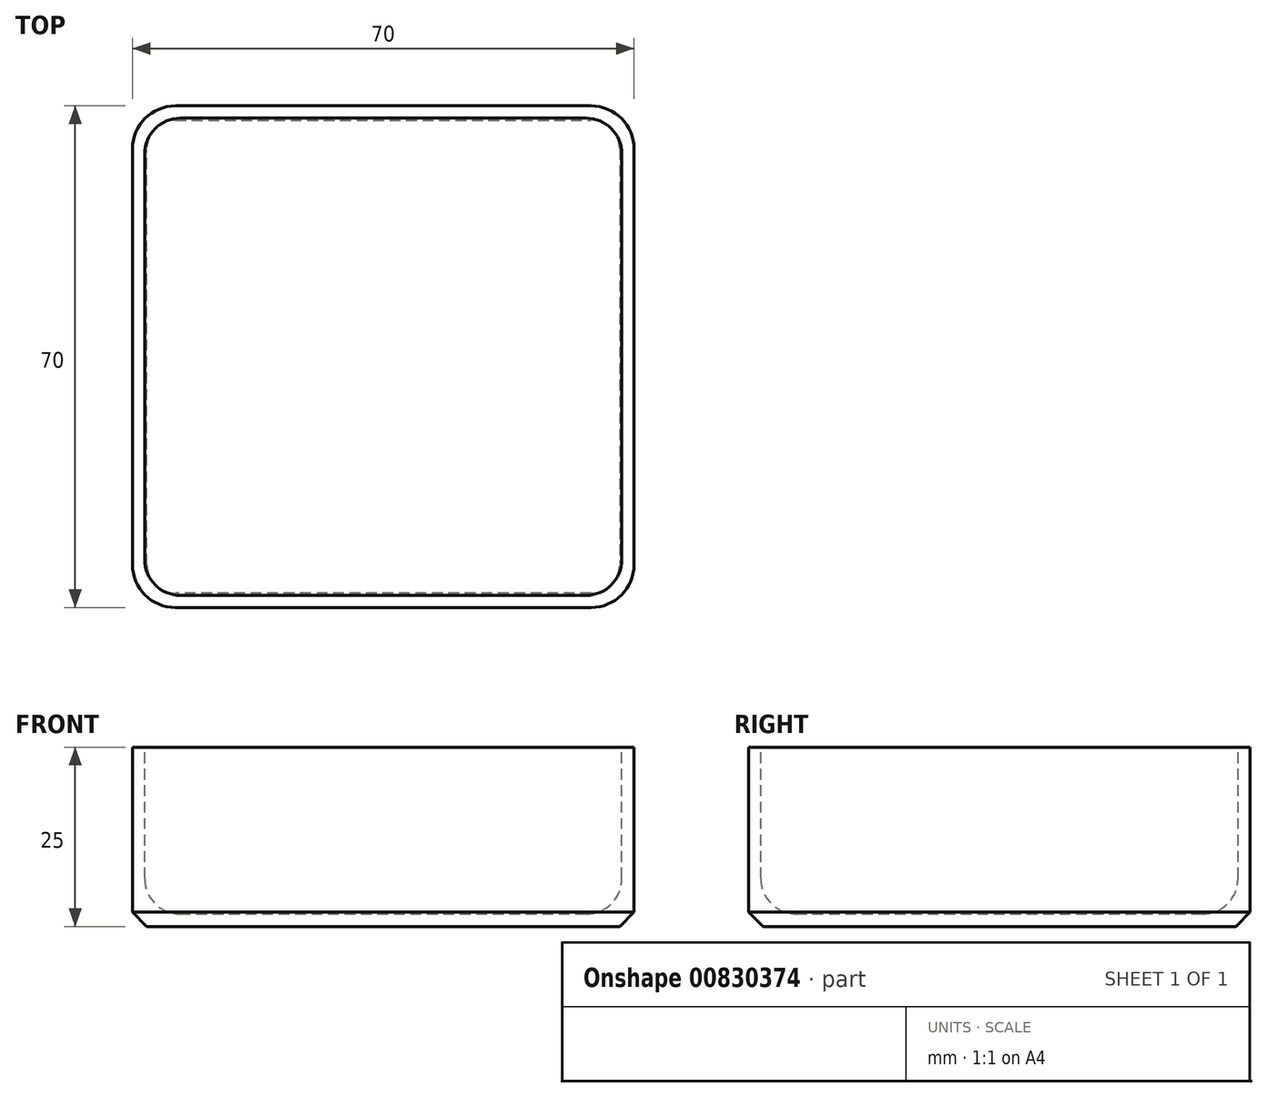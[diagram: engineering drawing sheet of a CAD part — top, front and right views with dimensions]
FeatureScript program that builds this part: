
annotation { "Feature Type Name" : "Feature", "Feature Type Description" : "" }
export const myFeature = defineFeature(function(context is Context, id is Id, definition is map)
    precondition{}
    {
        {
            var Q0;
            Q0=qCreatedBy(makeId("Top.planeOp"),FACE);
            var sketch = newSketch(context, id + "F0", { "sketchPlane" : qUnion([Q0])});
            skLineSegment(sketch, "E0.bottom", {"start": v(35, 35) * mm, "end": v(-35, 35) * mm});
            skLineSegment(sketch, "E0.top", {"start": v(35, -35) * mm, "end": v(-35, -35) * mm});
            skLineSegment(sketch, "E0.left", {"start": v(35, 35) * mm, "end": v(35, -35) * mm});
            skLineSegment(sketch, "E0.right", {"start": v(-35, 35) * mm, "end": v(-35, -35) * mm});
            skPoint(sketch, "E0.middle", {"position": v(0, 0) * mm});
            skLineSegment(sketch, "E1.bottom", {"start": v(33.3, 33.3) * mm, "end": v(-33.3, 33.3) * mm});
            skLineSegment(sketch, "E1.top", {"start": v(33.3, -33.3) * mm, "end": v(-33.3, -33.3) * mm});
            skLineSegment(sketch, "E1.left", {"start": v(33.3, 33.3) * mm, "end": v(33.3, -33.3) * mm});
            skLineSegment(sketch, "E1.right", {"start": v(-33.3, 33.3) * mm, "end": v(-33.3, -33.3) * mm});
            skSolve(sketch);
        }
        {
            var Q0;
            Q0=makeQuery(id+"F0.imprint","IMPRINT",FACE,{"disambiguationData":[TD([[makeQuery(id+"F0.imprint","IMPRINT",EDGE,{"derivedFrom":sQuery(id+"F0.wireOp",EDGE,"E1.bottom")}),1.0]])]});
            var Q1;
            Q1 = qSketchRegion(id + "F0", true);
            var Q2;
            Q2=makeQuery(id+"F0.imprint","IMPRINT",FACE,{"disambiguationData":[TD([[makeQuery(id+"F0.imprint","IMPRINT",EDGE,{"derivedFrom":sQuery(id+"F0.wireOp",EDGE,"E0.bottom")}),1.0]])]});
            extrude(context, id + "F1", {"entities" : qUnion([Q0, Q1, Q2]), "depth" : 25 * mm, "offsetDistance" : 25 * mm});
        }
        {
            var Q0;
            Q0=makeQuery(id+"F1.opExtrude","CAP_FACE",FACE,{"disambiguationData":[OSD([sQuery(id+"F0.wireOp",EDGE,"E0.bottom"),sQuery(id+"F0.wireOp",EDGE,"E0.top"),sQuery(id+"F0.wireOp",EDGE,"E0.left"),sQuery(id+"F0.wireOp",EDGE,"E0.right")])],"isStart":false});
            var sketch = newSketch(context, id + "F2", { "sketchPlane" : qUnion([Q0])});
            skLineSegment(sketch, "E2.bottom", {"start": v(33.3, 33.3) * mm, "end": v(-33.3, 33.3) * mm});
            skLineSegment(sketch, "E2.top", {"start": v(33.3, -33.3) * mm, "end": v(-33.3, -33.3) * mm});
            skLineSegment(sketch, "E2.left", {"start": v(33.3, 33.3) * mm, "end": v(33.3, -33.3) * mm});
            skLineSegment(sketch, "E2.right", {"start": v(-33.3, 33.3) * mm, "end": v(-33.3, -33.3) * mm});
            skPoint(sketch, "E2.middle", {"position": v(0, 0) * mm});
            skSolve(sketch);
        }
        {
            var Q0;
            Q0=makeQuery(id+"F2.imprint","IMPRINT",FACE,{"disambiguationData":[TD([[makeQuery(id+"F2.imprint","IMPRINT",EDGE,{"derivedFrom":sQuery(id+"F2.wireOp",EDGE,"E2.bottom")}),1.0]])]});
            extrude(context, id + "F3", {"entities" : qUnion([Q0]), "operationType" : NewBodyOperationType.REMOVE, "oppositeDirection" : true, "depth" : 23.3 * mm, "offsetDistance" : 25 * mm});
        }
        {
            var Q0;
            Q0=makeQuery(id+"F3.boolean.opBoolean","COPY",EDGE,{"derivedFrom":makeQuery(id+"F3.opExtrude","CAP_EDGE",EDGE,{"disambiguationData":[OSD([sQuery(id+"F2.wireOp",EDGE,"E2.right")])],"isStart":false})});
            var Q1;
            Q1=makeQuery(id+"F3.boolean.opBoolean","COPY",EDGE,{"derivedFrom":makeQuery(id+"F3.opExtrude","CAP_EDGE",EDGE,{"disambiguationData":[OSD([sQuery(id+"F2.wireOp",EDGE,"E2.left")])],"isStart":false})});
            var Q2;
            Q2=makeQuery(id+"F3.boolean.opBoolean","COPY",EDGE,{"derivedFrom":makeQuery(id+"F3.opExtrude","SWEPT_EDGE",EDGE,{"disambiguationData":[OSD([sQuery(id+"F2.wireOp",EDGE,"E2.bottom"),sQuery(id+"F2.wireOp",EDGE,"E2.right")])]})});
            var Q3;
            Q3=makeQuery(id+"F3.boolean.opBoolean","COPY",EDGE,{"derivedFrom":makeQuery(id+"F3.opExtrude","CAP_EDGE",EDGE,{"disambiguationData":[OSD([sQuery(id+"F2.wireOp",EDGE,"E2.bottom")])],"isStart":false})});
            var Q4;
            Q4=makeQuery(id+"F3.boolean.opBoolean","COPY",EDGE,{"derivedFrom":makeQuery(id+"F3.opExtrude","SWEPT_EDGE",EDGE,{"disambiguationData":[OSD([sQuery(id+"F2.wireOp",EDGE,"E2.top"),sQuery(id+"F2.wireOp",EDGE,"E2.right")])]})});
            var Q5;
            Q5=makeQuery(id+"F3.boolean.opBoolean","COPY",EDGE,{"derivedFrom":makeQuery(id+"F3.opExtrude","CAP_EDGE",EDGE,{"disambiguationData":[OSD([sQuery(id+"F2.wireOp",EDGE,"E2.top")])],"isStart":false})});
            var Q6;
            Q6=makeQuery(id+"F3.boolean.opBoolean","COPY",EDGE,{"derivedFrom":makeQuery(id+"F3.opExtrude","SWEPT_EDGE",EDGE,{"disambiguationData":[OSD([sQuery(id+"F2.wireOp",EDGE,"E2.top"),sQuery(id+"F2.wireOp",EDGE,"E2.left")])]})});
            var Q7;
            Q7=makeQuery(id+"F3.boolean.opBoolean","COPY",EDGE,{"derivedFrom":makeQuery(id+"F3.opExtrude","SWEPT_EDGE",EDGE,{"disambiguationData":[OSD([sQuery(id+"F2.wireOp",EDGE,"E2.bottom"),sQuery(id+"F2.wireOp",EDGE,"E2.left")])]})});
            fillet(context, id + "F4", {"entities" : qUnion([Q0, Q1, Q2, Q3, Q4, Q5, Q6, Q7]), "radius" : 5 * mm, "tangentPropagation" : true, "allowEdgeOverflow" : false});
        }
        {
            var Q0;
            Q0=makeQuery(id+"F1.opExtrude","SWEPT_EDGE",EDGE,{"disambiguationData":[OSD([sQuery(id+"F0.wireOp",EDGE,"E0.bottom"),sQuery(id+"F0.wireOp",EDGE,"E0.left")])]});
            var Q1;
            Q1=makeQuery(id+"F1.opExtrude","SWEPT_EDGE",EDGE,{"disambiguationData":[OSD([sQuery(id+"F0.wireOp",EDGE,"E0.bottom"),sQuery(id+"F0.wireOp",EDGE,"E0.right")])]});
            var Q2;
            Q2=makeQuery(id+"F1.opExtrude","SWEPT_EDGE",EDGE,{"disambiguationData":[OSD([sQuery(id+"F0.wireOp",EDGE,"E0.top"),sQuery(id+"F0.wireOp",EDGE,"E0.left")])]});
            var Q3;
            Q3=makeQuery(id+"F1.opExtrude","SWEPT_EDGE",EDGE,{"disambiguationData":[OSD([sQuery(id+"F0.wireOp",EDGE,"E0.top"),sQuery(id+"F0.wireOp",EDGE,"E0.right")])]});
            fillet(context, id + "F5", {"entities" : qUnion([Q0, Q1, Q2, Q3]), "radius" : 6 * mm, "tangentPropagation" : true, "allowEdgeOverflow" : false});
        }
        {
            var Q0;
            Q0=makeQuery(id+"F1.opExtrude","CAP_EDGE",EDGE,{"disambiguationData":[OSD([sQuery(id+"F0.wireOp",EDGE,"E0.left")])],"isStart":true});
            chamfer(context, id + "F6", {"entities" : qUnion([Q0]), "width" : 2 * mm, "tangentPropagation" : true});
        }
    });
